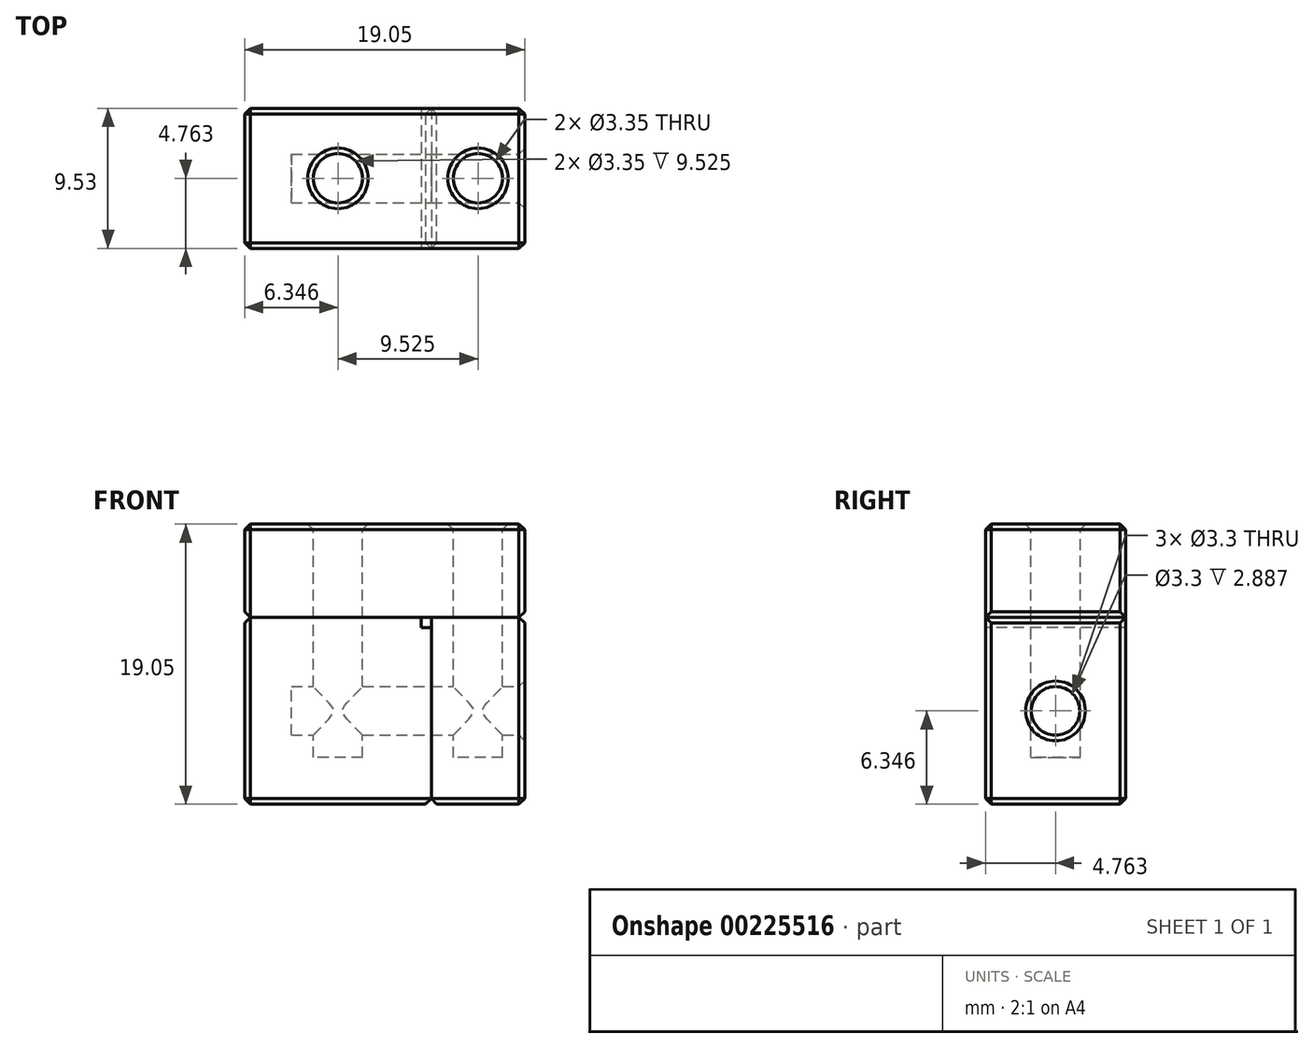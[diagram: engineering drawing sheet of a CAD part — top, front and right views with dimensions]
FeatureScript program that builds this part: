
annotation { "Feature Type Name" : "Feature", "Feature Type Description" : "" }
export const myFeature = defineFeature(function(context is Context, id is Id, definition is map)
    precondition{}
    {
        {
            var Q0;
            Q0=qCreatedBy(makeId("Front.planeOp"),FACE);
            var sketch = newSketch(context, id + "F0", { "sketchPlane" : qUnion([Q0])});
            skLineSegment(sketch, "E0", {"start": v(0, 0) * mm, "end": v(0, 0.69) * mm});
            skLineSegment(sketch, "E1", {"start": v(0, 0.69) * mm, "end": v(-12.01, 0.69) * mm});
            skLineSegment(sketch, "E2", {"start": v(-12.01, 0.69) * mm, "end": v(-12.01, -12.01) * mm});
            skLineSegment(sketch, "E3", {"start": v(-12.01, -12.01) * mm, "end": v(0.69, -12.01) * mm});
            skLineSegment(sketch, "E4", {"start": v(0.69, -12.01) * mm, "end": v(0.69, 0) * mm});
            skLineSegment(sketch, "E5", {"start": v(0.69, 0) * mm, "end": v(0, 0) * mm});
            skSolve(sketch);
        }
        {
            var Q0;
            Q0=makeQuery(id+"F0.imprint","IMPRINT",FACE,{"disambiguationData":[TD([[makeQuery(id+"F0.imprint","IMPRINT",EDGE,{"derivedFrom":sQuery(id+"F0.wireOp",EDGE,"E0")}),1.0]])]});
            extrude(context, id + "F1", {"entities" : qUnion([Q0]), "oppositeDirection" : true, "depth" : 9.52 * mm});
        }
        {
            var Q0;
            Q0=qCreatedBy(makeId("Front.planeOp"),FACE);
            var sketch = newSketch(context, id + "F2", { "sketchPlane" : qUnion([Q0])});
            skLineSegment(sketch, "E6.0.0", {"start": v(0.69, -12.01) * mm, "end": v(0.69, 0) * mm});
            skLineSegment(sketch, "E6.0.1", {"start": v(0.69, 0) * mm, "end": v(0, 0) * mm});
            skLineSegment(sketch, "E6.0.2", {"start": v(0, 0) * mm, "end": v(0, 0.69) * mm});
            skLineSegment(sketch, "E6.0.3", {"start": v(0, 0.69) * mm, "end": v(-12.01, 0.69) * mm});
            skLineSegment(sketch, "E6.0.4", {"start": v(-12.01, 0.69) * mm, "end": v(-12.01, -12.01) * mm});
            skLineSegment(sketch, "E6.0.5", {"start": v(-12.01, -12.01) * mm, "end": v(0.69, -12.01) * mm});
            skLineSegment(sketch, "E7", {"start": v(0.69, -12.01) * mm, "end": v(7.04, -12.01) * mm});
            skLineSegment(sketch, "E8", {"start": v(7.04, -12.01) * mm, "end": v(7.04, 0.69) * mm});
            skLineSegment(sketch, "E9", {"start": v(7.04, 0.69) * mm, "end": v(0.69, 0.69) * mm});
            skLineSegment(sketch, "E10", {"start": v(0.69, 0.69) * mm, "end": v(0.69, -12.01) * mm});
            skSolve(sketch);
        }
        {
            var Q0;
            {var subQ3=sQuery(id+"F2.wireOp",EDGE,"E7");Q0=makeQuery(id+"F2.imprint","IMPRINT",FACE,{"disambiguationData":[TD([[makeQuery(id+"F2.imprint","IMPRINT",EDGE,{"derivedFrom":subQ3}),1.0]])]});}
            extrude(context, id + "F3", {"entities" : qUnion([Q0]), "oppositeDirection" : true, "depth" : 9.52 * mm});
        }
        {
            var Q0;
            Q0=qCreatedBy(makeId("Front.planeOp"),FACE);
            var sketch = newSketch(context, id + "F4", { "sketchPlane" : qUnion([Q0])});
            skPoint(sketch, "E11.0", {"position": v(-12.01, 0.69) * mm});
            skPoint(sketch, "E12.0", {"position": v(7.04, 0.69) * mm});
            skLineSegment(sketch, "E13", {"start": v(-12.01, 0.69) * mm, "end": v(-12.01, 7.04) * mm});
            skLineSegment(sketch, "E14", {"start": v(-12.01, 7.04) * mm, "end": v(7.04, 7.04) * mm});
            skLineSegment(sketch, "E15", {"start": v(7.04, 7.04) * mm, "end": v(7.04, 0.69) * mm});
            skLineSegment(sketch, "E16", {"start": v(-12.01, 0.69) * mm, "end": v(7.04, 0.69) * mm});
            skSolve(sketch);
        }
        {
            var Q0;
            Q0=makeQuery(id+"F4.imprint","IMPRINT",FACE,{"disambiguationData":[TD([[makeQuery(id+"F4.imprint","IMPRINT",EDGE,{"derivedFrom":sQuery(id+"F4.wireOp",EDGE,"E13")}),-1.0]])]});
            extrude(context, id + "F5", {"entities" : qUnion([Q0]), "oppositeDirection" : true, "depth" : 9.52 * mm});
        }
        {
            var Q0;
            Q0=makeQuery(id+"F3.opExtrude","SWEPT_FACE",FACE,{"disambiguationData":[OSD([sQuery(id+"F2.wireOp",EDGE,"E8")])]});
            var sketch = newSketch(context, id + "F6", { "sketchPlane" : qUnion([Q0])});
            skCircle(sketch, "E17", {"center": v(4.76, -5.66) * mm, "radius": 1.65 * mm});
            skSolve(sketch);
        }
        {
            var Q0;
            Q0=makeQuery(id+"F6.imprint","IMPRINT",FACE,{"disambiguationData":[TD([[makeQuery(id+"F6.imprint","IMPRINT",EDGE,{"derivedFrom":sQuery(id+"F6.wireOp",EDGE,"E17")}),1.0]])]});
            extrude(context, id + "F7", {"entities" : qUnion([Q0]), "operationType" : NewBodyOperationType.REMOVE, "oppositeDirection" : true, "depth" : 15.88 * mm});
        }
        {
            var Q0;
            Q0=makeQuery(id+"F5.opExtrude","SWEPT_FACE",FACE,{"disambiguationData":[OSD([sQuery(id+"F4.wireOp",EDGE,"E14")])]});
            var sketch = newSketch(context, id + "F8", { "sketchPlane" : qUnion([Q0])});
            skCircle(sketch, "E18", {"center": v(-5.66, 4.76) * mm, "radius": 1.68 * mm});
            skCircle(sketch, "E19", {"center": v(3.86, 4.76) * mm, "radius": 1.68 * mm});
            skSolve(sketch);
        }
        {
            var Q0;
            Q0=makeQuery(id+"F8.imprint","IMPRINT",FACE,{"disambiguationData":[TD([[makeQuery(id+"F8.imprint","IMPRINT",EDGE,{"derivedFrom":sQuery(id+"F8.wireOp",EDGE,"E18")}),1.0]])]});
            var Q1;
            Q1=makeQuery(id+"F8.imprint","IMPRINT",FACE,{"disambiguationData":[TD([[makeQuery(id+"F8.imprint","IMPRINT",EDGE,{"derivedFrom":sQuery(id+"F8.wireOp",EDGE,"E19")}),1.0]])]});
            extrude(context, id + "F9", {"entities" : qUnion([Q0, Q1]), "operationType" : NewBodyOperationType.REMOVE, "oppositeDirection" : true, "depth" : 15.88 * mm});
        }
        {
            var Q0;
            Q0=makeQuery(id+"F5.opExtrude","CAP_EDGE",EDGE,{"disambiguationData":[OSD([sQuery(id+"F4.wireOp",EDGE,"E15")])],"isStart":true});
            var Q1;
            Q1=makeQuery(id+"F3.opExtrude","CAP_EDGE",EDGE,{"disambiguationData":[OSD([sQuery(id+"F2.wireOp",EDGE,"E8")])],"isStart":true});
            var Q2;
            Q2=makeQuery(id+"F3.opExtrude","CAP_EDGE",EDGE,{"disambiguationData":[OSD([sQuery(id+"F2.wireOp",EDGE,"E7")])],"isStart":true});
            var Q3;
            Q3=makeQuery(id+"F1.opExtrude","CAP_EDGE",EDGE,{"disambiguationData":[OSD([sQuery(id+"F0.wireOp",EDGE,"E3")])],"isStart":true});
            var Q4;
            Q4=makeQuery(id+"F1.opExtrude","CAP_EDGE",EDGE,{"disambiguationData":[OSD([sQuery(id+"F0.wireOp",EDGE,"E2")])],"isStart":true});
            var Q5;
            Q5=makeQuery(id+"F5.opExtrude","CAP_EDGE",EDGE,{"disambiguationData":[OSD([sQuery(id+"F4.wireOp",EDGE,"E13")])],"isStart":true});
            var Q6;
            Q6=makeQuery(id+"F5.opExtrude","SWEPT_FACE",FACE,{"disambiguationData":[OSD([sQuery(id+"F4.wireOp",EDGE,"E14")])]});
            var Q7;
            Q7=makeQuery(id+"F5.opExtrude","SWEPT_FACE",FACE,{"disambiguationData":[OSD([sQuery(id+"F4.wireOp",EDGE,"E15")])]});
            var Q8;
            Q8=makeQuery(id+"F3.opExtrude","SWEPT_FACE",FACE,{"disambiguationData":[OSD([sQuery(id+"F2.wireOp",EDGE,"E8")])]});
            var Q9;
            Q9=makeQuery(id+"F3.opExtrude","SWEPT_FACE",FACE,{"disambiguationData":[OSD([sQuery(id+"F2.wireOp",EDGE,"E7")])]});
            var Q10;
            Q10=makeQuery(id+"F1.opExtrude","SWEPT_FACE",FACE,{"disambiguationData":[OSD([sQuery(id+"F0.wireOp",EDGE,"E3")])]});
            var Q11;
            Q11=makeQuery(id+"F1.opExtrude","CAP_EDGE",EDGE,{"disambiguationData":[OSD([sQuery(id+"F0.wireOp",EDGE,"E2")])],"isStart":false});
            var Q12;
            Q12=makeQuery(id+"F5.opExtrude","SWEPT_FACE",FACE,{"disambiguationData":[OSD([sQuery(id+"F4.wireOp",EDGE,"E13")])]});
            var Q13;
            Q13=makeQuery(id+"F1.opExtrude","SWEPT_FACE",FACE,{"disambiguationData":[OSD([sQuery(id+"F0.wireOp",EDGE,"E2")])]});
            chamfer(context, id + "F10", {"entities" : qUnion([Q0, Q1, Q2, Q3, Q4, Q5, Q6, Q7, Q8, Q9, Q10, Q11, Q12, Q13]), "width" : 0.38 * mm, "tangentPropagation" : true});
        }
    });
